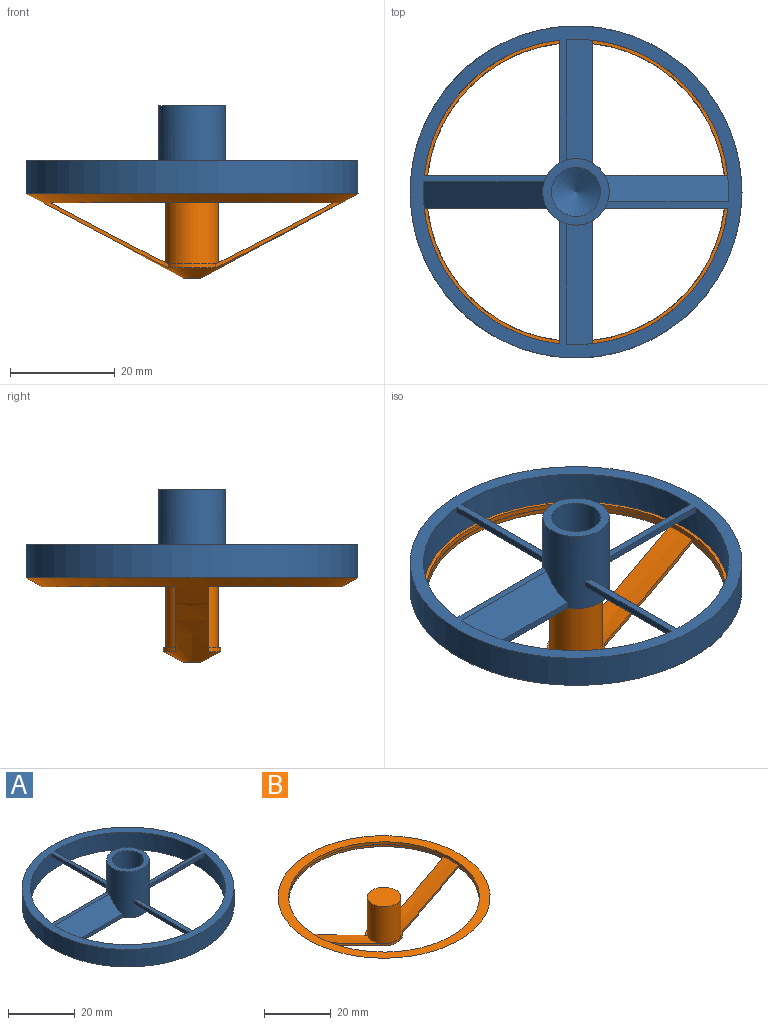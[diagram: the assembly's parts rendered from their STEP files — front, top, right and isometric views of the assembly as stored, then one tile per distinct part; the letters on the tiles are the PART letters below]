
ASSEMBLY  parts=2 mates=1
PART A: 28 faces, bbox 63.5x63.5x16.9 mm
  f0: plane 63.49x63.49mm, normal (0,0,-1), area 731.8mm2, adj f3,f4,f5,f8,f9,f10,f11,f12
  f1: plane 63.49x63.49mm, normal (0,0,1), area 604.9mm2, adj f3,f4,f6,f7,f8,f11,f13,f14
  f2: plane 12.71x12.71mm, normal (0,0,1), area 57.6mm2, adj f4,f26
  f3: cylinder r=31.74mm len=63.49mm, axis (0,0,-1), area 1266.7mm2, adj f0,f1
  f4: cylinder r=6.36mm len=16.92mm, axis (0,0,-1), area 613.3mm2, adj f0,f1,f2,f5,f6,f7,f9,f10
  f5: cylinder r=6.36mm len=1.91mm, axis (0,0,-1), area 1.8mm2, adj f0,f4,f21
  f6: plane 23.53x1.27mm, normal (-1,0,0), area 29.9mm2, adj f1,f4,f8,f18
  f7: plane 23.53x1.27mm, normal (0,1,0), area 29.9mm2, adj f1,f4,f8,f21
  f8: cylinder r=29.21mm len=31.11mm, axis (0,0,1), area 276.7mm2, adj f0,f1,f6,f7,f18,f21
  f9: plane 23.53x1.27mm, normal (0,1,0), area 29.9mm2, adj f0,f4,f11,f23
  f10: plane 23.53x1.27mm, normal (1,0,0), area 29.9mm2, adj f0,f4,f11,f22
  f11: cylinder r=29.21mm len=31.11mm, axis (0,0,1), area 276.7mm2, adj f0,f1,f9,f10,f22,f23
  f12: plane 23.53x1.27mm, normal (1,0,0), area 29.9mm2, adj f0,f4,f14,f24
  f13: plane 23.53x1.27mm, normal (0,-1,0), area 29.9mm2, adj f1,f4,f14,f19
  f14: cylinder r=29.21mm len=31.11mm, axis (0,0,1), area 276.7mm2, adj f0,f1,f12,f13,f19,f24
  f15: plane 23.53x1.27mm, normal (0,-1,0), area 29.9mm2, adj f0,f4,f17,f25
  f16: plane 23.53x1.27mm, normal (-1,0,0), area 29.9mm2, adj f1,f4,f17,f20
  f17: cylinder r=29.21mm len=31.11mm, axis (0,0,1), area 276.7mm2, adj f0,f1,f15,f16,f20,f25
  f18: plane 23.71x5.09mm, normal (-0.71,0,-0.71), area 165.3mm2, adj f0,f4,f6,f8
  f19: plane 23.71x5.09mm, normal (0,-0.71,-0.71), area 165.3mm2, adj f0,f4,f13,f14
  f20: plane 23.71x5.09mm, normal (-0.71,0,-0.71), area 165.3mm2, adj f0,f4,f16,f17
  f21: plane 23.71x5.09mm, normal (0,0.71,-0.71), area 165.3mm2, adj f0,f4,f5,f7,f8
  f22: plane 23.71x5.09mm, normal (0.71,0,0.71), area 165.3mm2, adj f1,f4,f10,f11
  f23: plane 23.71x5.09mm, normal (0,0.71,0.71), area 165.3mm2, adj f1,f4,f9,f11
  f24: plane 23.71x5.09mm, normal (0.71,0,0.71), area 165.3mm2, adj f1,f4,f12,f14
  f25: plane 23.71x5.09mm, normal (0,-0.71,0.71), area 165.3mm2, adj f1,f4,f15,f17
  f26: cylinder r=4.7mm len=9.4mm, axis (0,0,1), area 277.5mm2, adj f2,f27
  f27: cone r=0mm half-angle=59deg, axis (0,0,1), area 80.9mm2, adj f26
PART B: 16 faces, bbox 63.5x63.5x16.2 mm
  f0: cone r=5.05mm half-angle=61.9deg, axis (0,0,1), area 351.6mm2, adj f2,f3,f8,f9,f10,f11,f12,f13
  f1: cone r=1.57mm half-angle=61.8deg, axis (0,0,1), area 1116.9mm2, adj f6,f7,f8,f9,f10,f11,f12,f13
  f2: cylinder r=28.58mm len=57.16mm, axis (0,0,1), area 171mm2, adj f0,f7
  f3: cylinder r=5.05mm len=13.54mm, axis (0,0,1), area 429.3mm2, adj f0,f4
  f4: plane 10.09x10.09mm, normal (0,0,1), area 80mm2, adj f3
  f5: plane 3.13x3.13mm, normal (0,0,-1), area 7.7mm2, adj f6
  f6: cylinder r=1.57mm len=8.04mm, axis (0,0,1), area 79.2mm2, adj f1,f5
  f7: plane 63.51x63.51mm, normal (0,0,1), area 602.4mm2, adj f1,f2
  f8: cylinder r=5.48mm len=9.03mm, axis (0,0,1), area 8mm2, adj f0,f1,f9,f11
  f9: plane 23.87x13.1mm, normal (0,1,0), area 18mm2, adj f0,f1,f8,f10
  f10: cylinder r=28.55mm len=56.75mm, axis (0,0,1), area 62.5mm2, adj f0,f1,f9,f11
  f11: plane 23.87x13.1mm, normal (0,1,0), area 18mm2, adj f0,f1,f8,f10
  f12: cylinder r=5.48mm len=9.03mm, axis (0,0,1), area 8mm2, adj f0,f1,f13,f15
  f13: plane 23.87x13.1mm, normal (0,-1,0), area 18mm2, adj f0,f1,f12,f14
  f14: cylinder r=28.55mm len=56.75mm, axis (0,0,1), area 62.5mm2, adj f0,f1,f13,f15
  f15: plane 23.87x13.1mm, normal (0,-1,0), area 18mm2, adj f0,f1,f12,f14
PLACE A t=(-1.63,11.92,-3.97)mm
PLACE B t=(-1.63,11.92,-3.84)mm
MATE revolute A.f3 <-> B.f8  axis (0,0,-1) through (-1.63,11.92,-3.84)mm
